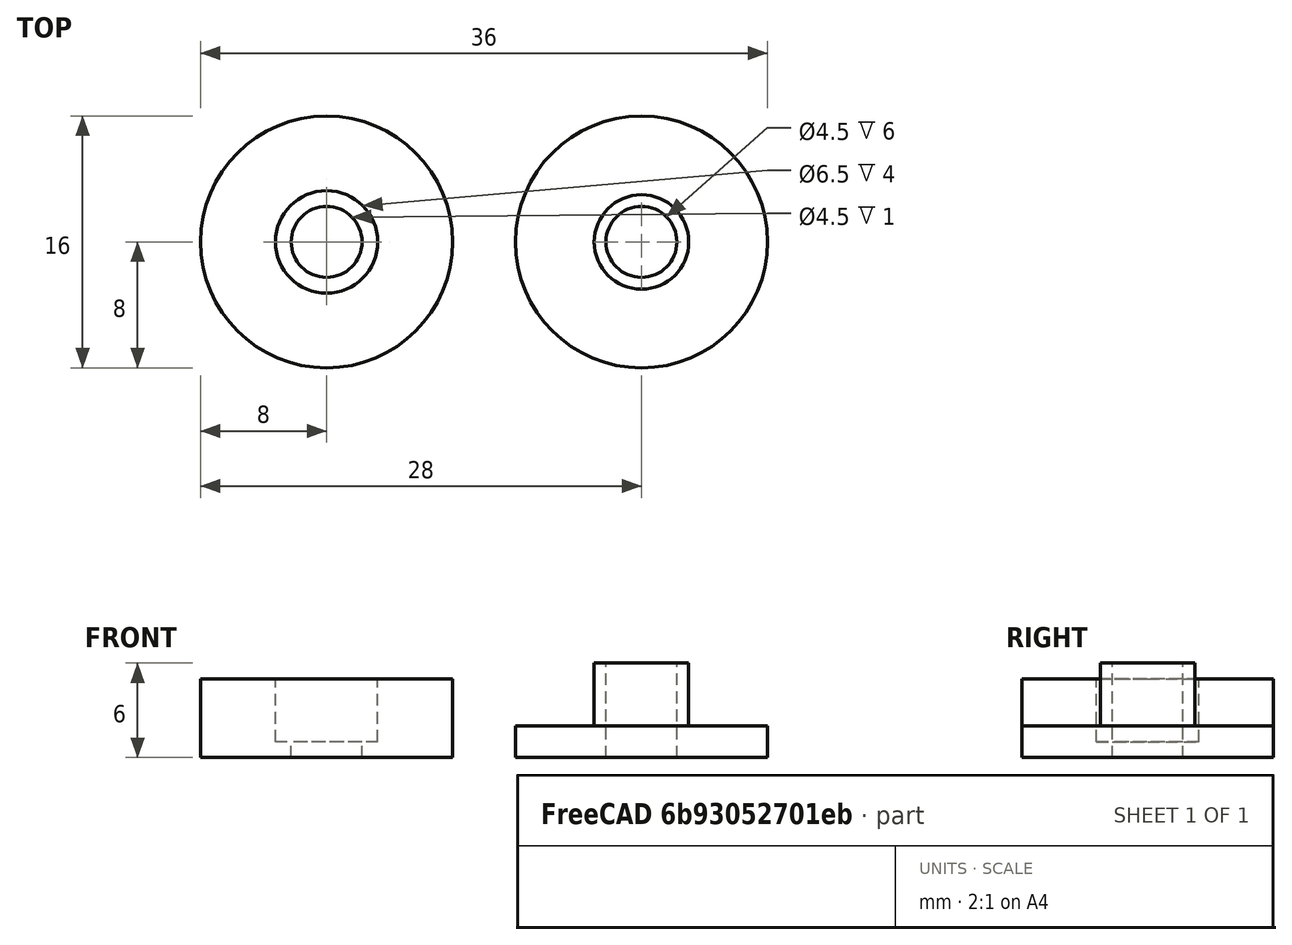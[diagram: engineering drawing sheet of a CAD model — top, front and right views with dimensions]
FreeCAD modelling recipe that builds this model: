
FCSTD DOCUMENT  (FreeCAD 0.19R)
Label: CaliperMount
License: All rights reserved
LicenseURL: http://en.wikipedia.org/wiki/All_rights_reserved
objects: Part::Cylinder×6, Part::MultiFuse×2, Part::Cut×2
note: 10 computed .brp shape members not serialized (recipe doc carries the construction recipe); baked Part::Feature solids carry a one-line shape summary decoded from their .brp

FEATURE [Part::Cylinder] Cylinder
  Angle = 360
  AttacherType = Attacher::AttachEngine3D
  Height = 5
  Radius = 8
FEATURE [Part::Cylinder] Cylinder001
  Angle = 360
  AttacherType = Attacher::AttachEngine3D
  Height = 9
  Placement = pos=(0,0,-0.5) rot=(0,0,1;0rad)
  Radius = 2.25
FEATURE [Part::Cylinder] Cylinder002
  Angle = 360
  AttacherType = Attacher::AttachEngine3D
  Height = 5
  Placement = pos=(0,0,1) rot=(0,0,1;0rad)
  Radius = 3.25
FEATURE [Part::MultiFuse] Fusion
  Shapes = -> [Cylinder001,Cylinder002]
FEATURE [Part::Cut] Cut  label="Body"
  Base = -> Cylinder
  Tool = -> Fusion
FEATURE [Part::Cylinder] Cylinder003
  Angle = 360
  AttacherType = Attacher::AttachEngine3D
  Height = 6
  Placement = pos=(20,0,0) rot=(0,0,1;0rad)
  Radius = 3
FEATURE [Part::Cylinder] Cylinder004
  Angle = 360
  AttacherType = Attacher::AttachEngine3D
  Height = 10
  Placement = pos=(20,0,0) rot=(0,0,1;0rad)
  Radius = 2.25
FEATURE [Part::Cylinder] Cylinder005
  Angle = 360
  AttacherType = Attacher::AttachEngine3D
  Height = 2
  Placement = pos=(20,0,0) rot=(0,0,1;0rad)
  Radius = 8
FEATURE [Part::MultiFuse] Fusion001
  Shapes = -> [Cylinder003,Cylinder005]
FEATURE [Part::Cut] Cut001  label="Cap"
  Base = -> Fusion001
  Tool = -> Cylinder004
